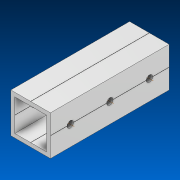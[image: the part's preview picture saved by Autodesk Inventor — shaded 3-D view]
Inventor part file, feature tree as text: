
AUTODESK INVENTOR PART (.ipt)
format: ipt  version: 2022.2 (Build 262287000, 287)  size: 635,904 bytes
history: native  units: in
note: dims shown in document units (in); Inventor stores cm internally (conversion verified against a paired STEP export)
features: other x3, extrude x1, pattern_linear x1, sketch x1, pattern_circular x1
ambient origin geometry x8: Origin, YZ Plane, XZ Plane, XY Plane, X Axis, Y Axis, Z Axis, Center Point
bodies: Solid1 (feature_tree)
feature tree (7):
  extrude  "Extrusion1"  Depth=1.0in
  other  "Work Axis1"
  pattern_linear  "Rectangular Pattern1"  Spacing1=0.0in  [1 undecoded]
  sketch  "Sketch1"  dims[d0=1.0in d1=56.0in d2=0.0in d3=1.1811in d5=1.0in]
  other  "Work Axis2"
  other  "Work Axis3"
  pattern_circular  "CirPattern2"
note: 1 required parameter value undecoded (feature->parameter linkage not recoverable at this tier; creation-order binding heuristic only, values carry confidence <= 0.55)
